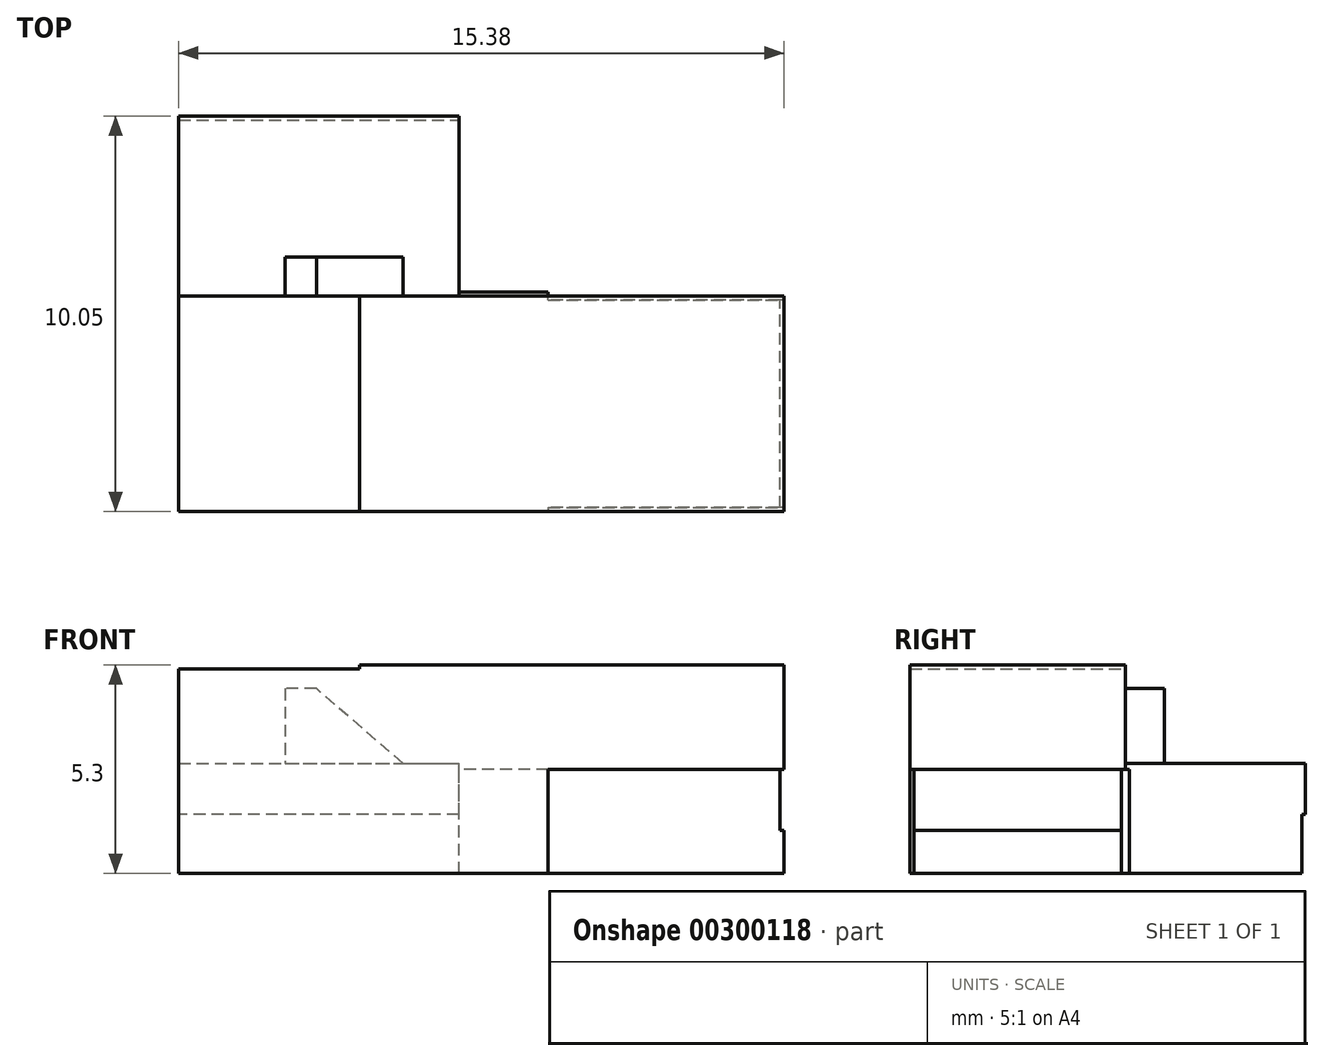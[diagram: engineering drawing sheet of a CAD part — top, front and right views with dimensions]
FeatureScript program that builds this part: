
annotation { "Feature Type Name" : "Feature", "Feature Type Description" : "" }
export const myFeature = defineFeature(function(context is Context, id is Id, definition is map)
    precondition{}
    {
        {
            var Q0;
            Q0=qCreatedBy(makeId("Top.planeOp"),FACE);
            var sketch = newSketch(context, id + "F0", { "sketchPlane" : qUnion([Q0])});
            skLineSegment(sketch, "E0.bottom", {"start": v(0, 0) * mm, "end": v(15.38, 0) * mm});
            skLineSegment(sketch, "E0.top", {"start": v(0, 5.47) * mm, "end": v(15.38, 5.47) * mm});
            skLineSegment(sketch, "E0.left", {"start": v(0, 0) * mm, "end": v(0, 5.47) * mm});
            skLineSegment(sketch, "E0.right", {"start": v(15.38, 0) * mm, "end": v(15.38, 5.47) * mm});
            skSolve(sketch);
        }
        {
            var Q0;
            Q0 = qSketchRegion(id + "F0", true);
            extrude(context, id + "F1", {"entities" : qUnion([Q0]), "depth" : (.3 + 2.35 + .2 + 2.25 + .2) * mm});
        }
        {
            var Q0;
            Q0=makeQuery(id+"F1.opExtrude","SWEPT_FACE",FACE,{"disambiguationData":[OSD([sQuery(id+"F0.wireOp",EDGE,"E0.top")])]});
            var sketch = newSketch(context, id + "F2", { "sketchPlane" : qUnion([Q0])});
            skLineSegment(sketch, "E1.bottom", {"start": v(0, 0) * mm, "end": v(-7.12, 0) * mm});
            skLineSegment(sketch, "E1.top", {"start": v(0, 2.8) * mm, "end": v(-7.12, 2.8) * mm});
            skLineSegment(sketch, "E1.left", {"start": v(0, 0) * mm, "end": v(0, 2.8) * mm});
            skLineSegment(sketch, "E1.right", {"start": v(-7.12, 0) * mm, "end": v(-7.12, 2.8) * mm});
            skSolve(sketch);
        }
        {
            var Q0;
            Q0 = qSketchRegion(id + "F2", true);
            extrude(context, id + "F3", {"entities" : qUnion([Q0]), "operationType" : NewBodyOperationType.ADD, "depth" : (4.11 + .47) * mm});
        }
        {
            var Q0;
            Q0=makeQuery(id+"F1.opExtrude","SWEPT_FACE",FACE,{"disambiguationData":[OSD([sQuery(id+"F0.wireOp",EDGE,"E0.top")])]});
            var sketch = newSketch(context, id + "F4", { "sketchPlane" : qUnion([Q0])});
            skLineSegment(sketch, "E2", {"start": v(-5.7, 2.8) * mm, "end": v(-3.5, 4.7) * mm});
            skLineSegment(sketch, "E3", {"start": v(-3.5, 4.7) * mm, "end": v(-2.7, 4.7) * mm});
            skLineSegment(sketch, "E4", {"start": v(-2.7, 4.7) * mm, "end": v(-2.7, 2.8) * mm});
            skLineSegment(sketch, "E5", {"start": v(-2.7, 2.8) * mm, "end": v(-5.7, 2.8) * mm});
            skSolve(sketch);
        }
        {
            var Q0;
            Q0 = qSketchRegion(id + "F4", true);
            extrude(context, id + "F5", {"entities" : qUnion([Q0]), "operationType" : NewBodyOperationType.ADD, "depth" : 1 * mm});
        }
        {
            var Q0;
            Q0=makeQuery(id+"F1.opExtrude","CAP_FACE",FACE,{"disambiguationData":[OSD([sQuery(id+"F0.wireOp",EDGE,"E0.bottom"),sQuery(id+"F0.wireOp",EDGE,"E0.top"),sQuery(id+"F0.wireOp",EDGE,"E0.left"),sQuery(id+"F0.wireOp",EDGE,"E0.right")])],"isStart":false});
            var sketch = newSketch(context, id + "F6", { "sketchPlane" : qUnion([Q0])});
            skLineSegment(sketch, "E6.bottom", {"start": v(0, 5.47) * mm, "end": v(4.6, 5.47) * mm});
            skLineSegment(sketch, "E6.top", {"start": v(0, 0) * mm, "end": v(4.6, 0) * mm});
            skLineSegment(sketch, "E6.left", {"start": v(0, 5.47) * mm, "end": v(0, 0) * mm});
            skLineSegment(sketch, "E6.right", {"start": v(4.6, 5.47) * mm, "end": v(4.6, 0) * mm});
            skSolve(sketch);
        }
        {
            var Q0;
            Q0 = qSketchRegion(id + "F6", true);
            extrude(context, id + "F7", {"entities" : qUnion([Q0]), "operationType" : NewBodyOperationType.REMOVE, "oppositeDirection" : true, "depth" : .1 * mm});
        }
        {
            var Q0;
            Q0=makeQuery(id+"F1.opExtrude","SWEPT_FACE",FACE,{"disambiguationData":[OSD([sQuery(id+"F0.wireOp",EDGE,"E0.top")])]});
            var sketch = newSketch(context, id + "F8", { "sketchPlane" : qUnion([Q0])});
            skLineSegment(sketch, "E7.bottom", {"start": v(-15.38, 0) * mm, "end": v(-9.4, 0) * mm});
            skLineSegment(sketch, "E7.top", {"start": v(-15.38, 2.65) * mm, "end": v(-9.4, 2.65) * mm});
            skLineSegment(sketch, "E7.left", {"start": v(-15.38, 0) * mm, "end": v(-15.38, 2.65) * mm});
            skLineSegment(sketch, "E7.right", {"start": v(-9.4, 0) * mm, "end": v(-9.4, 2.65) * mm});
            skSolve(sketch);
        }
        {
            var Q0;
            Q0 = qSketchRegion(id + "F8", true);
            extrude(context, id + "F9", {"entities" : qUnion([Q0]), "operationType" : NewBodyOperationType.REMOVE, "oppositeDirection" : true, "depth" : .1 * mm});
        }
        {
            var Q0;
            Q0=makeQuery(id+"F1.opExtrude","SWEPT_FACE",FACE,{"disambiguationData":[OSD([sQuery(id+"F0.wireOp",EDGE,"E0.right")])]});
            var sketch = newSketch(context, id + "F10", { "sketchPlane" : qUnion([Q0])});
            skLineSegment(sketch, "E8.bottom", {"start": v(0, 1.1) * mm, "end": v(5.47, 1.1) * mm});
            skLineSegment(sketch, "E8.top", {"start": v(0, 2.65) * mm, "end": v(5.47, 2.65) * mm});
            skLineSegment(sketch, "E8.left", {"start": v(0, 1.1) * mm, "end": v(0, 2.65) * mm});
            skLineSegment(sketch, "E8.right", {"start": v(5.47, 1.1) * mm, "end": v(5.47, 2.65) * mm});
            skSolve(sketch);
        }
        {
            var Q0;
            Q0 = qSketchRegion(id + "F10", true);
            extrude(context, id + "F11", {"entities" : qUnion([Q0]), "operationType" : NewBodyOperationType.REMOVE, "oppositeDirection" : true, "depth" : .1 * mm});
        }
        {
            var Q0;
            Q0=makeQuery(id+"F1.opExtrude","SWEPT_FACE",FACE,{"disambiguationData":[OSD([sQuery(id+"F0.wireOp",EDGE,"E0.bottom")])]});
            var sketch = newSketch(context, id + "F12", { "sketchPlane" : qUnion([Q0])});
            skLineSegment(sketch, "E9.bottom", {"start": v(15.38, 2.65) * mm, "end": v(9.4, 2.65) * mm});
            skLineSegment(sketch, "E9.top", {"start": v(15.38, 0) * mm, "end": v(9.4, 0) * mm});
            skLineSegment(sketch, "E9.left", {"start": v(15.38, 2.65) * mm, "end": v(15.38, 0) * mm});
            skLineSegment(sketch, "E9.right", {"start": v(9.4, 2.65) * mm, "end": v(9.4, 0) * mm});
            skSolve(sketch);
        }
        {
            var Q0;
            Q0 = qSketchRegion(id + "F12", true);
            extrude(context, id + "F13", {"entities" : qUnion([Q0]), "operationType" : NewBodyOperationType.REMOVE, "oppositeDirection" : true, "depth" : .1 * mm});
        }
        {
            var Q0;
            Q0=makeQuery(id+"F3.opExtrude","CAP_FACE",FACE,{"disambiguationData":[OSD([sQuery(id+"F2.wireOp",EDGE,"E1.bottom"),sQuery(id+"F2.wireOp",EDGE,"E1.top"),sQuery(id+"F2.wireOp",EDGE,"E1.left"),sQuery(id+"F2.wireOp",EDGE,"E1.right")])],"isStart":false});
            var sketch = newSketch(context, id + "F14", { "sketchPlane" : qUnion([Q0])});
            skLineSegment(sketch, "E10.bottom", {"start": v(-7.12, 0) * mm, "end": v(0, 0) * mm});
            skLineSegment(sketch, "E10.top", {"start": v(-7.12, 1.5) * mm, "end": v(0, 1.5) * mm});
            skLineSegment(sketch, "E10.left", {"start": v(-7.12, 0) * mm, "end": v(-7.12, 1.5) * mm});
            skLineSegment(sketch, "E10.right", {"start": v(0, 0) * mm, "end": v(0, 1.5) * mm});
            skSolve(sketch);
        }
        {
            var Q0;
            Q0 = qSketchRegion(id + "F14", true);
            extrude(context, id + "F15", {"entities" : qUnion([Q0]), "operationType" : NewBodyOperationType.REMOVE, "oppositeDirection" : true, "depth" : .1 * mm});
        }
        {
            var Q0;
            Q0=makeQuery(id+"F1.opExtrude","SWEPT_FACE",FACE,{"disambiguationData":[OSD([sQuery(id+"F0.wireOp",EDGE,"E0.top")])]});
            var sketch = newSketch(context, id + "F16", { "sketchPlane" : qUnion([Q0])});
            skLineSegment(sketch, "E11.bottom", {"start": v(-9.4, 2.65) * mm, "end": v(-7.12, 2.65) * mm});
            skLineSegment(sketch, "E11.top", {"start": v(-9.4, 0) * mm, "end": v(-7.12, 0) * mm});
            skLineSegment(sketch, "E11.left", {"start": v(-9.4, 2.65) * mm, "end": v(-9.4, 0) * mm});
            skLineSegment(sketch, "E11.right", {"start": v(-7.12, 2.65) * mm, "end": v(-7.12, 0) * mm});
            skSolve(sketch);
        }
        {
            var Q0;
            Q0 = qSketchRegion(id + "F16", true);
            extrude(context, id + "F17", {"entities" : qUnion([Q0]), "operationType" : NewBodyOperationType.ADD, "depth" : .1 * mm});
        }
    });
